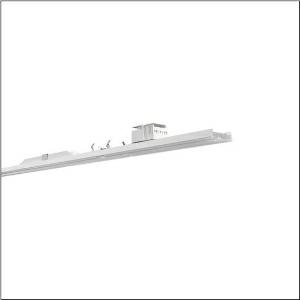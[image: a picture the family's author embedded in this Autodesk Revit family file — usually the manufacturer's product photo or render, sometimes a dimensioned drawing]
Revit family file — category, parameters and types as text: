
# Revit family: licross_r__21_recessed_ho_51tl12dn4gxld_90f8
name_source: partatom
category: Lighting Fixtures
units: mm (PartAtom-declared; Revit-internal decimal feet)

## family parameters
Cut with Voids When Loaded = No
Host = Face
Light Source = No
Part Type = Normal
Room Calculation Point = No
Round Connector Dimension = Use Diameter
Shared = No

## types (1)
- --- (1 x LED, 2460 lm, 15.5 W, 4000K)
    Apparent Load = 16 VA
    CIE Flux Codes = 66 91 98 100 100
    Color Rendering = 80
    Color Temperature = 4000K
    Default Elevation = 1800 mm
    Description = Licross® 21 Recessed HO, luminaire insert, of sheet steel, galvanised, coil coated, white, length: 1.500mm, width: 66mm, height: 67mm, LED rated luminous flux: 16.080lm, light colour: 840, control gear: DALI 2, control gear: ECG DALI, with plug, 6-pole, with phase selection, mains connection: 220..240V, AC/DC, 0/50..60Hz, halogen-free wiring, for central battery installations according to DIN EN 60598-2-22, for emergency light function, without changeover relay, primary optical cover: cover, of PMMA, light emission: direct distribution, protection rating (complete): IP40, insulation class (complete): insulation class I (protective earthing), certification: CE, ENEC, VDE, UKCA, protection symbol: D if used in an environment without relevant dust loads with corresponding accessories, permissible ambient temperature for indoor applications: 0..+25°C, standard: EN 60598-2-22, corresponds to IFS (International Featured Standards) requirements for safety and quality in the food industry, reducing of maximum allowable ambient temperature of 5°C with ceiling mounting, LABS conformity tested according to VDMA 24364:2018-05, packaging unit: 1 piece
    Height = 58 mm
    Lamp = 1 x LED
    Lamp Light Flux = 2460 lm
    Lamp Power = 15.5 W
    Lamp count = 1
    Length = 1500 mm
    Luminous efficacy = 159 lm/W
    Manufacturer = Siteco
    ModVariant = No
    Model = 51TL12DN4GXLD
    Mounting Place = Ceiling
    Mounting Type = Pendant
    Number of Poles = 1
    OnlyDefault = Yes
    Power Factor = 1
    Product Name = Licross® 21 Recessed HO
    Product group = luminaire insert
    ProductGroupID = 902
    Protection Class = Protection class I
    Protection Degree = IP 40
    RLX_Detail_Level = 1
    RlxData = <blob elided: 22909 chars, md5=82ec7615>
    Socket = socket
    Standby Power = 0 W
    System Light Flux = 2460 lm
    System Power = 16 W
    Type Comments = : DC mode (central or group accumulator) initial emergency light level
    Type Image = l_1266722.jpg
    URL = http://relux.com
    VarID = @adj_121305
    Voltage = 0 V
    Weight = 0.00 kg
    Width = 66 mm

## geometry (parser evidence)
native form markers: Blend x4, Sweep x10
no freeform markers — native parametric forms only
